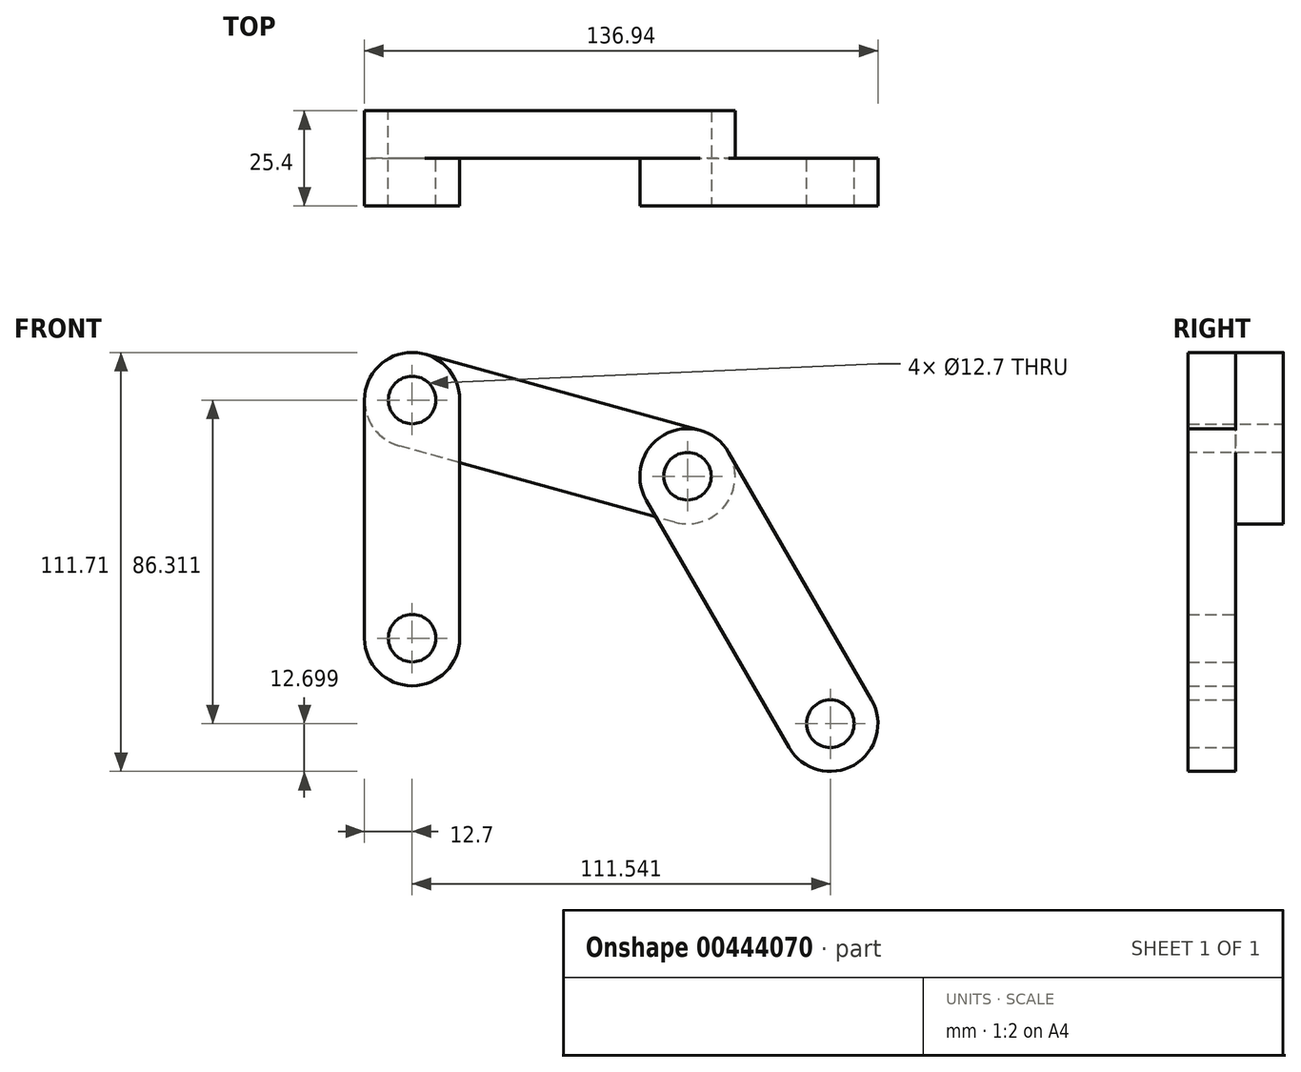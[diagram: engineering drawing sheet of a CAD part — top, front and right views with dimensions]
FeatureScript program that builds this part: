
annotation { "Feature Type Name" : "Feature", "Feature Type Description" : "" }
export const myFeature = defineFeature(function(context is Context, id is Id, definition is map)
    precondition{}
    {
        {
            var Q0;
            Q0=qCreatedBy(makeId("Front.planeOp"),FACE);
            var sketch = newSketch(context, id + "F0", { "sketchPlane" : qUnion([Q0])});
            skCircle(sketch, "E0", {"center": v(0, 0) * mm, "radius": 12.7 * mm});
            skCircle(sketch, "E1", {"center": v(0, 0) * mm, "radius": 6.35 * mm});
            skCircle(sketch, "E2", {"center": v(0, -63.5) * mm, "radius": 12.7 * mm});
            skCircle(sketch, "E3", {"center": v(0, -63.5) * mm, "radius": 6.35 * mm});
            skLineSegment(sketch, "E4", {"start": v(-12.7, 0) * mm, "end": v(-12.7, -63.5) * mm});
            skLineSegment(sketch, "E5", {"start": v(12.7, 0) * mm, "end": v(12.7, -63.5) * mm});
            skSolve(sketch);
        }
        {
            var Q0;
            Q0 = qSketchRegion(id + "F0", true);
            extrude(context, id + "F1", {"entities" : qUnion([Q0]), "depth" : 12.7 * mm});
        }
        {
            var Q0;
            Q0=makeQuery(id+"F1.opExtrude","CAP_FACE",FACE,{"disambiguationData":[OSD([sQuery(id+"F0.wireOp",EDGE,"E0"),sQuery(id+"F0.wireOp",EDGE,"E1"),sQuery(id+"F0.wireOp",EDGE,"E2"),sQuery(id+"F0.wireOp",EDGE,"E3"),sQuery(id+"F0.wireOp",EDGE,"E4"),sQuery(id+"F0.wireOp",EDGE,"E5")])],"isStart":true});
            var sketch = newSketch(context, id + "F2", { "sketchPlane" : qUnion([Q0])});
            skCircle(sketch, "E6", {"center": v(0, 0) * mm, "radius": 12.7 * mm});
            skCircle(sketch, "E7", {"center": v(0, 0) * mm, "radius": 6.35 * mm});
            skCircle(sketch, "E8", {"center": v(-73.44, -20.32) * mm, "radius": 12.7 * mm});
            skCircle(sketch, "E9", {"center": v(-73.44, -20.32) * mm, "radius": 6.35 * mm});
            skLineSegment(sketch, "E10", {"start": v(-76.83, -8.08) * mm, "end": v(-3.39, 12.24) * mm});
            skLineSegment(sketch, "E11", {"start": v(-70.05, -32.56) * mm, "end": v(3.39, -12.24) * mm});
            skSolve(sketch);
        }
        {
            var Q0;
            Q0 = qSketchRegion(id + "F2", true);
            extrude(context, id + "F3", {"entities" : qUnion([Q0]), "operationType" : NewBodyOperationType.ADD, "depth" : 12.7 * mm});
        }
        {
            var Q0;
            Q0=makeQuery(id+"F3.opExtrude","CAP_FACE",FACE,{"disambiguationData":[OSD([sQuery(id+"F2.wireOp",EDGE,"E6"),sQuery(id+"F2.wireOp",EDGE,"E7"),sQuery(id+"F2.wireOp",EDGE,"E8"),sQuery(id+"F2.wireOp",EDGE,"E9"),sQuery(id+"F2.wireOp",EDGE,"E10"),sQuery(id+"F2.wireOp",EDGE,"E11")])],"isStart":true});
            var sketch = newSketch(context, id + "F4", { "sketchPlane" : qUnion([Q0])});
            skCircle(sketch, "E12", {"center": v(73.44, -20.32) * mm, "radius": 12.7 * mm});
            skCircle(sketch, "E13", {"center": v(73.44, -20.32) * mm, "radius": 6.35 * mm});
            skCircle(sketch, "E14", {"center": v(111.54, -86.31) * mm, "radius": 12.7 * mm});
            skCircle(sketch, "E15", {"center": v(111.54, -86.31) * mm, "radius": 6.35 * mm});
            skLineSegment(sketch, "E16", {"start": v(62.44, -26.67) * mm, "end": v(100.54, -92.66) * mm});
            skLineSegment(sketch, "E17", {"start": v(84.44, -13.97) * mm, "end": v(122.54, -79.96) * mm});
            skSolve(sketch);
        }
        {
            var Q0;
            Q0 = qSketchRegion(id + "F4", true);
            extrude(context, id + "F5", {"entities" : qUnion([Q0]), "operationType" : NewBodyOperationType.ADD, "depth" : 12.7 * mm});
        }
    });
